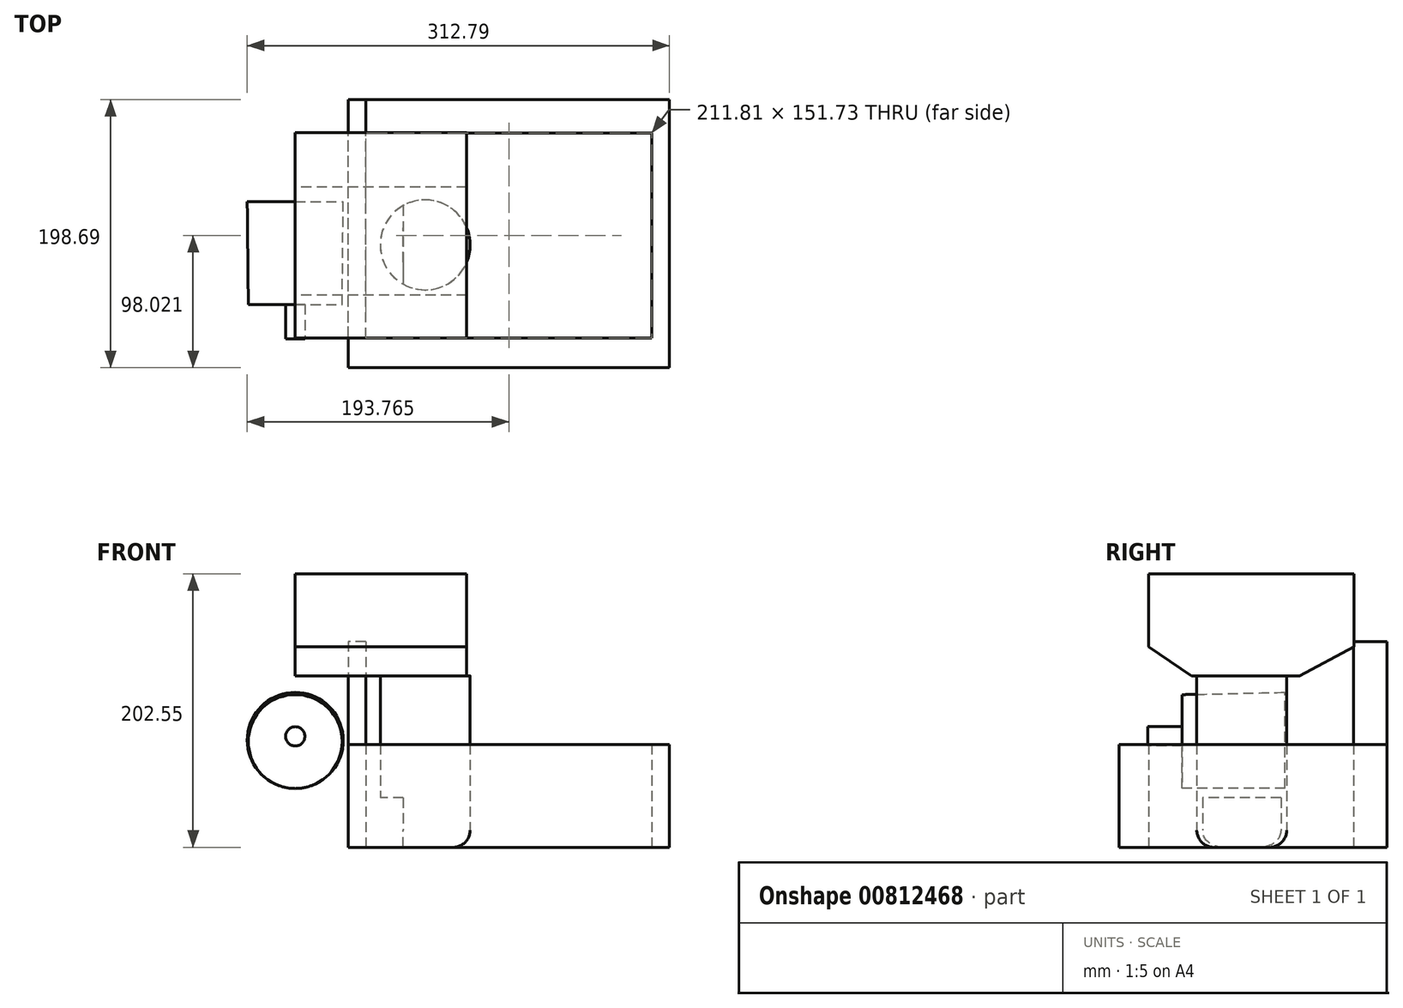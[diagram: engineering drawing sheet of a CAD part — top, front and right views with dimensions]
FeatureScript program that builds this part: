
annotation { "Feature Type Name" : "Feature", "Feature Type Description" : "" }
export const myFeature = defineFeature(function(context is Context, id is Id, definition is map)
    precondition{}
    {
        {
            var Q0;
            Q0=qCreatedBy(makeId("Right.planeOp"),FACE);
            var sketch = newSketch(context, id + "F0", { "sketchPlane" : qUnion([Q0])});
            skLineSegment(sketch, "E0", {"start": v(36.2, 0) * mm, "end": v(76.54, 21.32) * mm});
            skLineSegment(sketch, "E1", {"start": v(76.54, 21.32) * mm, "end": v(76.54, 75.55) * mm});
            skLineSegment(sketch, "E2", {"start": v(76.54, 75.55) * mm, "end": v(-75.55, 75.55) * mm});
            skLineSegment(sketch, "E3", {"start": v(-75.55, 75.55) * mm, "end": v(-75.55, 21.32) * mm});
            skLineSegment(sketch, "E4", {"start": v(-75.55, 21.32) * mm, "end": v(-43.8, 0) * mm});
            skLineSegment(sketch, "E5", {"start": v(-43.8, 0) * mm, "end": v(36.2, 0) * mm});
            skSolve(sketch);
        }
        {
            var Q0;
            Q0=makeQuery(id+"F0.imprint","IMPRINT",FACE,{"disambiguationData":[TD([[makeQuery(id+"F0.imprint","IMPRINT",EDGE,{"derivedFrom":sQuery(id+"F0.wireOp",EDGE,"E0")}),1.0]])]});
            extrude(context, id + "F1", {"entities" : qUnion([Q0]), "depth" : 127 * mm, "offsetDistance" : 25.4 * mm});
        }
        {
            var Q0;
            Q0=makeQuery(id+"F1.opExtrude","SWEPT_FACE",FACE,{"disambiguationData":[OSD([sQuery(id+"F0.wireOp",EDGE,"E5")])]});
            var sketch = newSketch(context, id + "F2", { "sketchPlane" : qUnion([Q0])});
            skSolve(sketch);
        }
        {
            var Q0;
            {var subQ0=sQuery(id+"F0.wireOp",EDGE,"E5");Q0=makeQuery(id+"F2.imprint","IMPRINT",FACE,{"disambiguationData":[TD([[makeQuery(id+"F2.imprint","IMPRINT",EDGE,{"derivedFrom":makeQuery(id+"F1.opExtrude","CAP_EDGE",EDGE,{"disambiguationData":[OSD([subQ0])],"isStart":true})}),1.0]])]});}
            cPlane(context, id + "F3", {"entities" : qUnion([Q0]), "cplaneType" : CPlaneType.OFFSET, "offset" : 127 * mm, "width" : 152.4 * mm, "height" : 152.4 * mm});
        }
        {
            var Q0;
            Q0=qCreatedBy(id+"F3.planeOp",FACE);
            var sketch = newSketch(context, id + "F4", { "sketchPlane" : qUnion([Q0])});
            skCircle(sketch, "E6", {"center": v(96.25, 6.66) * mm, "radius": 33.3 * mm});
            skSolve(sketch);
        }
        {
            var Q0;
            Q0=makeQuery(id+"F4.imprint","IMPRINT",FACE,{"disambiguationData":[TD([[makeQuery(id+"F4.imprint","IMPRINT",EDGE,{"derivedFrom":sQuery(id+"F4.wireOp",EDGE,"E6")}),1.0]])]});
            extrude(context, id + "F5", {"entities" : qUnion([Q0]), "operationType" : NewBodyOperationType.ADD, "oppositeDirection" : true, "depth" : 127 * mm, "offsetDistance" : 25.4 * mm});
        }
        {
            var Q0;
            Q0=makeQuery(id+"F5.opExtrude","CAP_EDGE",EDGE,{"disambiguationData":[OSD([sQuery(id+"F4.wireOp",EDGE,"E6")])],"isStart":true});
            fillet(context, id + "F6", {"entities" : qUnion([Q0]), "radius" : 12.7 * mm, "tangentPropagation" : true, "allowEdgeOverflow" : false});
        }
        {
            var Q0;
            Q0=qCreatedBy(makeId("Right.planeOp"),FACE);
            var sketch = newSketch(context, id + "F7", { "sketchPlane" : qUnion([Q0])});
            skLineSegment(sketch, "E7.bottom", {"start": v(-53.97, -60.41) * mm, "end": v(41.6, -60.41) * mm});
            skLineSegment(sketch, "E7.top", {"start": v(-53.97, -74.23) * mm, "end": v(41.6, -74.23) * mm});
            skLineSegment(sketch, "E7.left", {"start": v(-53.97, -60.41) * mm, "end": v(-53.97, -74.23) * mm});
            skLineSegment(sketch, "E7.right", {"start": v(41.6, -60.41) * mm, "end": v(41.6, -74.23) * mm});
            skSolve(sketch);
        }
        {
            var Q0;
            Q0=makeQuery(id+"F7.imprint","IMPRINT",FACE,{"disambiguationData":[TD([[makeQuery(id+"F7.imprint","IMPRINT",EDGE,{"derivedFrom":sQuery(id+"F7.wireOp",EDGE,"E7.bottom")}),-1.0]])]});
            extrude(context, id + "F8", {"entities" : qUnion([Q0]), "depth" : 76.2 * mm, "offsetDistance" : 25.4 * mm});
        }
        {
            var Q0;
            Q0=qCreatedBy(makeId("Front.planeOp"),FACE);
            var sketch = newSketch(context, id + "F9", { "sketchPlane" : qUnion([Q0])});
            skLineSegment(sketch, "E8.bottom", {"start": v(79.97, -90.36) * mm, "end": v(0, -90.36) * mm});
            skLineSegment(sketch, "E8.top", {"start": v(79.97, -136.42) * mm, "end": v(0, -136.42) * mm});
            skLineSegment(sketch, "E8.left", {"start": v(79.97, -90.36) * mm, "end": v(79.97, -136.42) * mm});
            skLineSegment(sketch, "E8.right", {"start": v(0, -90.36) * mm, "end": v(0, -136.42) * mm});
            skSolve(sketch);
        }
        {
            var Q0;
            Q0=makeQuery(id+"F9.imprint","IMPRINT",FACE,{"disambiguationData":[TD([[makeQuery(id+"F9.imprint","IMPRINT",EDGE,{"derivedFrom":sQuery(id+"F9.wireOp",EDGE,"E8.bottom")}),1.0]])]});
            extrude(context, id + "F10", {"entities" : qUnion([Q0]), "operationType" : NewBodyOperationType.REMOVE, "oppositeDirection" : true, "depth" : 76.2 * mm, "offsetDistance" : 25.4 * mm});
        }
        {
            var Q0;
            Q0=makeQuery(id+"F10.boolean.opBoolean","COPY",FACE,{"derivedFrom":makeQuery(id+"F10.opExtrude","CAP_FACE",FACE,{"disambiguationData":[OSD([sQuery(id+"F9.wireOp",EDGE,"E8.bottom"),sQuery(id+"F9.wireOp",EDGE,"E8.top"),sQuery(id+"F9.wireOp",EDGE,"E8.left"),sQuery(id+"F9.wireOp",EDGE,"E8.right")])],"isStart":true})});
            extrude(context, id + "F11", {"entities" : qUnion([Q0]), "operationType" : NewBodyOperationType.REMOVE, "endBound" : BoundingType.UP_TO_NEXT, "oppositeDirection" : true, "depth" : 25.4 * mm, "offsetDistance" : 25.4 * mm});
        }
        {
            var Q0;
            {var subQ0=sQuery(id+"F9.wireOp",EDGE,"E8.left");Q0=makeQuery(id+"F11.boolean.opBoolean","MERGE",FACE,{"derivedFrom":[makeQuery(id+"F10.boolean.opBoolean","COPY",FACE,{"derivedFrom":makeQuery(id+"F10.opExtrude","SWEPT_FACE",FACE,{"disambiguationData":[OSD([subQ0])]})}),makeQuery(id+"F11.opExtrude","SWEPT_FACE",FACE,{"disambiguationData":[OSD([subQ0])]})]});}
            extrude(context, id + "F12", {"entities" : qUnion([Q0]), "operationType" : NewBodyOperationType.REMOVE, "depth" : 25.4 * mm, "offsetDistance" : 25.4 * mm});
        }
        {
            var Q0;
            Q0=makeQuery(id+"F8.opExtrude","SWEPT_BODY",BODY,{"disambiguationData":[OSD([sQuery(id+"F7.wireOp",EDGE,"E7.bottom"),sQuery(id+"F7.wireOp",EDGE,"E7.top"),sQuery(id+"F7.wireOp",EDGE,"E7.left"),sQuery(id+"F7.wireOp",EDGE,"E7.right")])]});
            deleteBodies(context, id + "F13", {"entities" : qUnion([Q0])});
        }
        {
            var Q0;
            Q0=qCreatedBy(makeId("Front.planeOp"),FACE);
            cPlane(context, id + "F14", {"entities" : qUnion([Q0]), "cplaneType" : CPlaneType.OFFSET, "offset" : 50.8 * mm, "width" : 152.4 * mm, "height" : 152.4 * mm});
        }
        {
            var Q0;
            Q0=qCreatedBy(id+"F14.planeOp",FACE);
            var sketch = newSketch(context, id + "F15", { "sketchPlane" : qUnion([Q0])});
            skCircle(sketch, "E9", {"center": v(0, -48.73) * mm, "radius": 34.74 * mm});
            skSolve(sketch);
        }
        {
            var Q0;
            Q0=qCreatedBy(makeId("Front.planeOp"),FACE);
            cPlane(context, id + "F16", {"entities" : qUnion([Q0]), "cplaneType" : CPlaneType.OFFSET, "offset" : 25.4 * mm, "oppositeDirection" : true, "width" : 152.4 * mm, "height" : 152.4 * mm});
        }
        {
            var Q0;
            Q0=qCreatedBy(id+"F16.planeOp",FACE);
            var sketch = newSketch(context, id + "F17", { "sketchPlane" : qUnion([Q0])});
            skCircle(sketch, "E10", {"center": v(0, -47.84) * mm, "radius": 35.57 * mm});
            skSolve(sketch);
        }
        {
            var Q0;
            Q0=makeQuery(id+"F17.imprint","IMPRINT",FACE,{"disambiguationData":[TD([[makeQuery(id+"F17.imprint","IMPRINT",EDGE,{"derivedFrom":sQuery(id+"F17.wireOp",EDGE,"E10")}),1.0]])]});
            var Q1;
            Q1=makeQuery(id+"F15.imprint","IMPRINT",FACE,{"disambiguationData":[TD([[makeQuery(id+"F15.imprint","IMPRINT",EDGE,{"derivedFrom":sQuery(id+"F15.wireOp",EDGE,"E9")}),1.0]])]});
            loft(context, id + "F18", {"sheetProfilesArray" : [{ "sheetProfileEntities" : qUnion([Q0]) }, { "sheetProfileEntities" : qUnion([Q1]) }]});
        }
        {
            var Q0;
            Q0=qCreatedBy(id+"F14.planeOp",FACE);
            cPlane(context, id + "F19", {"entities" : qUnion([Q0]), "cplaneType" : CPlaneType.OFFSET, "offset" : 25.4 * mm, "width" : 152.4 * mm, "height" : 152.4 * mm});
        }
        {
            var Q0;
            Q0=qCreatedBy(id+"F19.planeOp",FACE);
            var sketch = newSketch(context, id + "F20", { "sketchPlane" : qUnion([Q0])});
            skCircle(sketch, "E11", {"center": v(0, -44.87) * mm, "radius": 7.13 * mm});
            skSolve(sketch);
        }
        {
            var Q0;
            Q0=makeQuery(id+"F20.imprint","IMPRINT",FACE,{"disambiguationData":[TD([[makeQuery(id+"F20.imprint","IMPRINT",EDGE,{"derivedFrom":sQuery(id+"F20.wireOp",EDGE,"E11")}),1.0]])]});
            extrude(context, id + "F21", {"entities" : qUnion([Q0]), "oppositeDirection" : true, "depth" : 25.4 * mm, "offsetDistance" : 25.4 * mm});
        }
        {
            var Q0;
            Q0=qCreatedBy(id+"F3.planeOp",FACE);
            var sketch = newSketch(context, id + "F22", { "sketchPlane" : qUnion([Q0])});
            skLineSegment(sketch, "E12.bottom", {"start": v(39.17, 97.63) * mm, "end": v(277.22, 97.63) * mm});
            skLineSegment(sketch, "E12.top", {"start": v(39.17, -101.06) * mm, "end": v(277.22, -101.06) * mm});
            skLineSegment(sketch, "E12.left", {"start": v(39.17, 97.63) * mm, "end": v(39.17, -101.06) * mm});
            skLineSegment(sketch, "E12.right", {"start": v(277.22, 97.63) * mm, "end": v(277.22, -101.06) * mm});
            skLineSegment(sketch, "E13.bottom", {"start": v(52.29, 75.48) * mm, "end": v(264.1, 75.48) * mm});
            skLineSegment(sketch, "E13.top", {"start": v(52.29, -76.26) * mm, "end": v(264.1, -76.26) * mm});
            skLineSegment(sketch, "E13.left", {"start": v(52.29, 75.48) * mm, "end": v(52.29, -76.26) * mm});
            skLineSegment(sketch, "E13.right", {"start": v(264.1, 75.48) * mm, "end": v(264.1, -76.26) * mm});
            skSolve(sketch);
        }
        {
            var Q0;
            Q0=makeQuery(id+"F22.imprint","IMPRINT",FACE,{"disambiguationData":[TD([[makeQuery(id+"F22.imprint","IMPRINT",EDGE,{"derivedFrom":sQuery(id+"F22.wireOp",EDGE,"E12.bottom")}),-1.0]])]});
            extrude(context, id + "F23", {"entities" : qUnion([Q0]), "oppositeDirection" : true, "depth" : 76.2 * mm, "offsetDistance" : 25.4 * mm});
        }
        {
            var Q0;
            Q0=makeQuery(id+"F23.opExtrude","CAP_FACE",FACE,{"disambiguationData":[OSD([sQuery(id+"F22.wireOp",EDGE,"E12.bottom"),sQuery(id+"F22.wireOp",EDGE,"E12.top"),sQuery(id+"F22.wireOp",EDGE,"E12.left"),sQuery(id+"F22.wireOp",EDGE,"E12.right"),sQuery(id+"F22.wireOp",EDGE,"E13.bottom"),sQuery(id+"F22.wireOp",EDGE,"E13.top"),sQuery(id+"F22.wireOp",EDGE,"E13.left"),sQuery(id+"F22.wireOp",EDGE,"E13.right")])],"isStart":false});
            var sketch = newSketch(context, id + "F24", { "sketchPlane" : qUnion([Q0])});
            skLineSegment(sketch, "E14.bottom", {"start": v(52.29, 76.26) * mm, "end": v(39.17, 76.26) * mm});
            skLineSegment(sketch, "E14.top", {"start": v(52.29, 101.06) * mm, "end": v(39.17, 101.06) * mm});
            skLineSegment(sketch, "E14.left", {"start": v(52.29, 76.26) * mm, "end": v(52.29, 101.06) * mm});
            skLineSegment(sketch, "E14.right", {"start": v(39.17, 76.26) * mm, "end": v(39.17, 101.06) * mm});
            skSolve(sketch);
        }
        {
            var Q0;
            Q0=makeQuery(id+"F24.imprint","IMPRINT",FACE,{"disambiguationData":[TD([[makeQuery(id+"F24.imprint","IMPRINT",EDGE,{"derivedFrom":sQuery(id+"F24.wireOp",EDGE,"E14.bottom")}),-1.0]])]});
            extrude(context, id + "F25", {"entities" : qUnion([Q0]), "depth" : 76.2 * mm, "offsetDistance" : 25.4 * mm});
        }
    });
